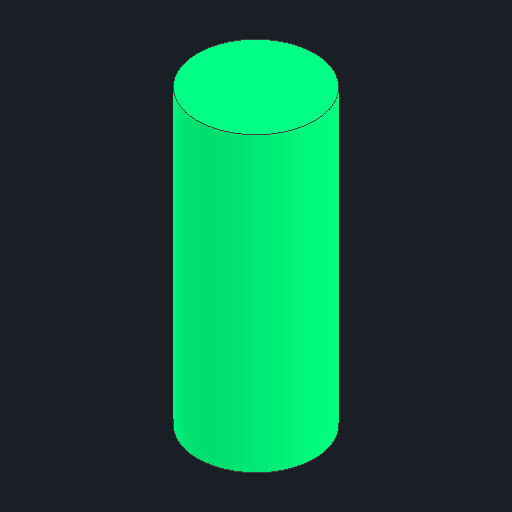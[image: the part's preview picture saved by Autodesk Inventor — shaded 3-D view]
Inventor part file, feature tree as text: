
AUTODESK INVENTOR PART (.ipt)
format: ipt  version: 2025.2 (Build 292293000, 293)  size: 83,456 bytes
history: native  units: in
note: dims shown in document units (in); Inventor stores cm internally (conversion verified against a paired STEP export)
features: other x3, sketch x1
ambient origin geometry x8: Origin, YZ Plane, XZ Plane, XY Plane, X Axis, Y Axis, Z Axis, Center Point
bodies: Solid1 (feature_tree)
feature tree (4):
  other  "26650(Green)_MIR1.ipt"
  other  "Solid1::26650(Green)_MIR1.ipt"
  other  "TaggingFeature1"
  sketch  "Sketch1"  dims[d0=0.3937in]
